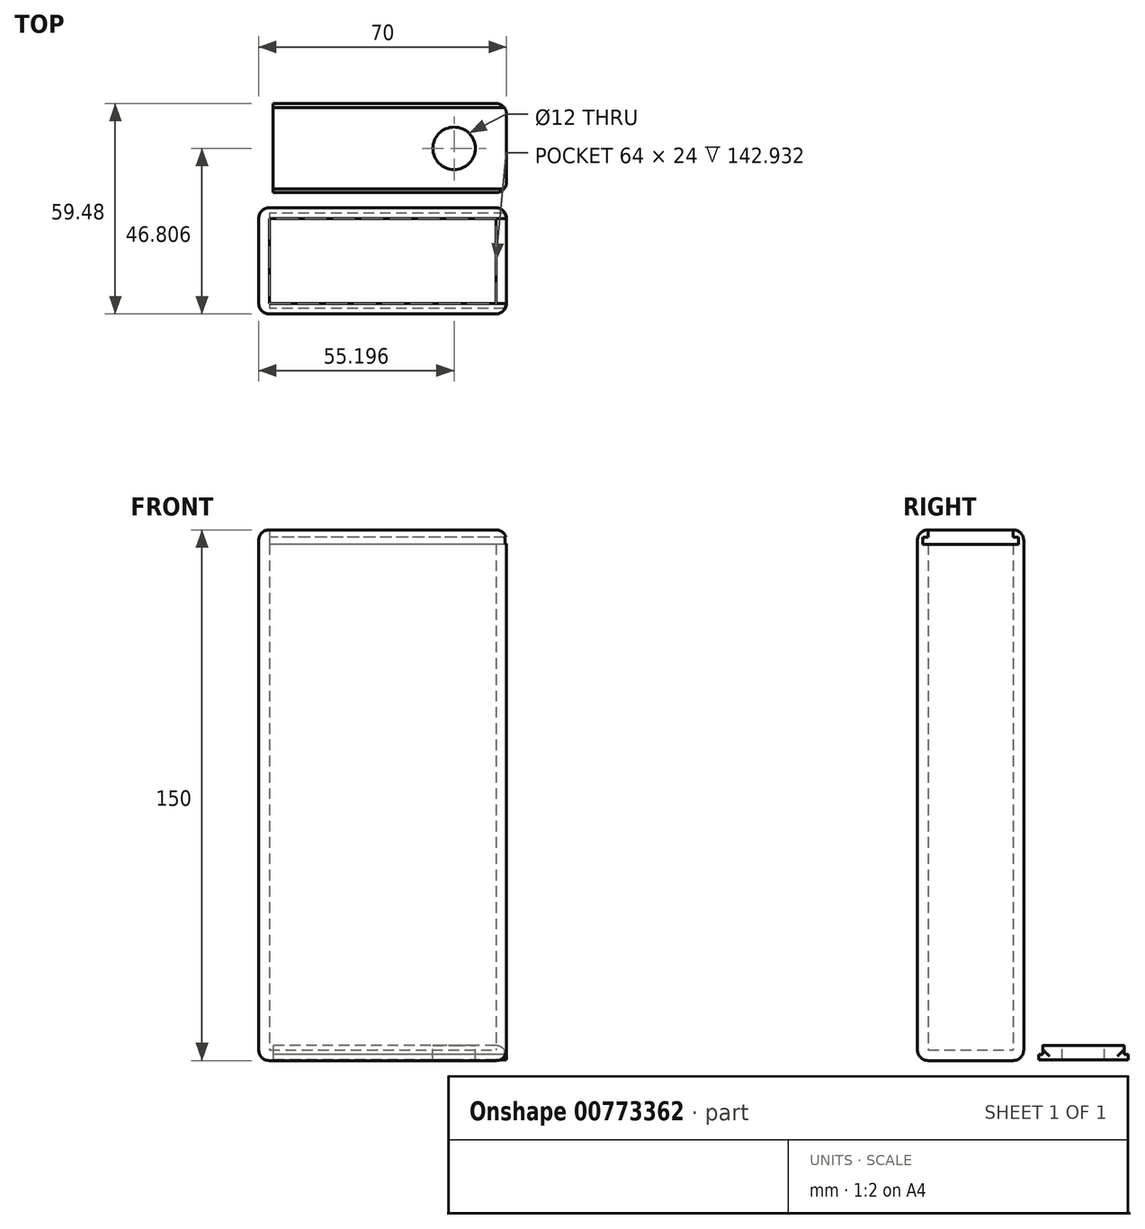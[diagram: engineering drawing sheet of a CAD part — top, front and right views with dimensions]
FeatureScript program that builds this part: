
annotation { "Feature Type Name" : "Feature", "Feature Type Description" : "" }
export const myFeature = defineFeature(function(context is Context, id is Id, definition is map)
    precondition{}
    {
        {
            var Q0;
            Q0=qCreatedBy(makeId("Top.planeOp"),FACE);
            var sketch = newSketch(context, id + "F0", { "sketchPlane" : qUnion([Q0])});
            skLineSegment(sketch, "E0.bottom", {"start": v(-35, -15) * mm, "end": v(35, -15) * mm});
            skLineSegment(sketch, "E0.top", {"start": v(-35, 15) * mm, "end": v(35, 15) * mm});
            skLineSegment(sketch, "E0.left", {"start": v(-35, -15) * mm, "end": v(-35, 15) * mm});
            skLineSegment(sketch, "E0.right", {"start": v(35, -15) * mm, "end": v(35, 15) * mm});
            skPoint(sketch, "E0.middle", {"position": v(0, 0) * mm});
            skSolve(sketch);
        }
        {
            var Q0;
            Q0 = qSketchRegion(id + "F0", true);
            extrude(context, id + "F1", {"entities" : qUnion([Q0]), "depth" : 150 * mm, "offsetDistance" : 25 * mm});
        }
        {
            var Q0;
            Q0=makeQuery(id+"F1.opExtrude","CAP_FACE",FACE,{"disambiguationData":[OSD([sQuery(id+"F0.wireOp",EDGE,"E0.bottom"),sQuery(id+"F0.wireOp",EDGE,"E0.top"),sQuery(id+"F0.wireOp",EDGE,"E0.left"),sQuery(id+"F0.wireOp",EDGE,"E0.right")])],"isStart":false});
            shell(context, id + "F2", {"entities" : qUnion([Q0]), "thickness" : 3 * mm});
        }
        {
            var Q0;
            Q0=qCreatedBy(makeId("Right.planeOp"),FACE);
            var sketch = newSketch(context, id + "F3", { "sketchPlane" : qUnion([Q0])});
            skLineSegment(sketch, "E1.bottom", {"start": v(12, 150.47) * mm, "end": v(-12, 150.47) * mm});
            skLineSegment(sketch, "E1.top", {"start": v(12, 147.47) * mm, "end": v(-12, 147.47) * mm});
            skLineSegment(sketch, "E1.left", {"start": v(12, 150.47) * mm, "end": v(12, 147.47) * mm});
            skLineSegment(sketch, "E1.right", {"start": v(-12, 150.47) * mm, "end": v(-12, 147.47) * mm});
            skPoint(sketch, "E1.middle", {"position": v(0, 148.97) * mm});
            skLineSegment(sketch, "E2.bottom", {"start": v(13.5, 147.93) * mm, "end": v(-13.5, 147.93) * mm});
            skLineSegment(sketch, "E2.top", {"start": v(13.5, 145.93) * mm, "end": v(-13.5, 145.93) * mm});
            skLineSegment(sketch, "E2.left", {"start": v(13.5, 147.93) * mm, "end": v(13.5, 145.93) * mm});
            skLineSegment(sketch, "E2.right", {"start": v(-13.5, 147.93) * mm, "end": v(-13.5, 145.93) * mm});
            skPoint(sketch, "E2.middle", {"position": v(0, 146.93) * mm});
            skSolve(sketch);
        }
        {
            var Q0;
            Q0 = qSketchRegion(id + "F3", true);
            extrude(context, id + "F4", {"entities" : qUnion([Q0]), "operationType" : NewBodyOperationType.REMOVE, "depth" : 36.4 * mm, "offsetDistance" : 25 * mm, "hasSecondDirection" : true, "secondDirectionOppositeDirection" : true, "secondDirectionDepth" : 32 * mm});
        }
        {
            var Q0;
            Q0=makeQuery(id+"F1.opExtrude","SWEPT_EDGE",EDGE,{"disambiguationData":[OSD([sQuery(id+"F0.wireOp",EDGE,"E0.top"),sQuery(id+"F0.wireOp",EDGE,"E0.right")])]});
            var Q1;
            Q1=makeQuery(id+"F1.opExtrude","SWEPT_EDGE",EDGE,{"disambiguationData":[OSD([sQuery(id+"F0.wireOp",EDGE,"E0.bottom"),sQuery(id+"F0.wireOp",EDGE,"E0.right")])]});
            var Q2;
            Q2=makeQuery(id+"F1.opExtrude","CAP_EDGE",EDGE,{"disambiguationData":[OSD([sQuery(id+"F0.wireOp",EDGE,"E0.right")])],"isStart":true});
            var Q3;
            Q3=makeQuery(id+"F1.opExtrude","CAP_FACE",FACE,{"disambiguationData":[OSD([sQuery(id+"F0.wireOp",EDGE,"E0.bottom"),sQuery(id+"F0.wireOp",EDGE,"E0.top"),sQuery(id+"F0.wireOp",EDGE,"E0.left"),sQuery(id+"F0.wireOp",EDGE,"E0.right")])],"isStart":true});
            var Q4;
            Q4=makeQuery(id+"F1.opExtrude","SWEPT_EDGE",EDGE,{"disambiguationData":[OSD([sQuery(id+"F0.wireOp",EDGE,"E0.top"),sQuery(id+"F0.wireOp",EDGE,"E0.left")])]});
            var Q5;
            Q5=makeQuery(id+"F1.opExtrude","SWEPT_EDGE",EDGE,{"disambiguationData":[OSD([sQuery(id+"F0.wireOp",EDGE,"E0.bottom"),sQuery(id+"F0.wireOp",EDGE,"E0.left")])]});
            fillet(context, id + "F5", {"entities" : qUnion([Q0, Q1, Q2, Q3, Q4, Q5]), "radius" : 3 * mm, "tangentPropagation" : true, "allowEdgeOverflow" : false});
        }
        {
            var Q0;
            Q0=makeQuery(id+"F1.opExtrude","CAP_EDGE",EDGE,{"disambiguationData":[OSD([sQuery(id+"F0.wireOp",EDGE,"E0.bottom")])],"isStart":false});
            fillet(context, id + "F6", {"entities" : qUnion([Q0]), "radius" : 3 * mm, "tangentPropagation" : true, "allowEdgeOverflow" : false});
        }
        {
            var Q0;
            Q0=qCreatedBy(makeId("Right.planeOp"),FACE);
            var sketch = newSketch(context, id + "F7", { "sketchPlane" : qUnion([Q0])});
            skLineSegment(sketch, "E3.bottom", {"start": v(43.38, 4.22) * mm, "end": v(20.38, 4.22) * mm});
            skLineSegment(sketch, "E3.top", {"start": v(43.38, 1.62) * mm, "end": v(20.38, 1.62) * mm});
            skLineSegment(sketch, "E3.left", {"start": v(43.38, 4.22) * mm, "end": v(43.38, 1.62) * mm});
            skLineSegment(sketch, "E3.right", {"start": v(20.38, 4.22) * mm, "end": v(20.38, 1.62) * mm});
            skPoint(sketch, "E3.middle", {"position": v(31.88, 2.92) * mm});
            skLineSegment(sketch, "E4.bottom", {"start": v(44.48, 1.67) * mm, "end": v(19.28, 1.67) * mm});
            skLineSegment(sketch, "E4.top", {"start": v(44.48, 0.27) * mm, "end": v(19.28, 0.27) * mm});
            skLineSegment(sketch, "E4.left", {"start": v(44.48, 1.67) * mm, "end": v(44.48, 0.27) * mm});
            skLineSegment(sketch, "E4.right", {"start": v(19.28, 1.67) * mm, "end": v(19.28, 0.27) * mm});
            skPoint(sketch, "E4.middle", {"position": v(31.88, 0.97) * mm});
            skSolve(sketch);
        }
        {
            var Q0;
            Q0 = qSketchRegion(id + "F7", true);
            extrude(context, id + "F8", {"entities" : qUnion([Q0]), "depth" : 35 * mm, "offsetDistance" : 25 * mm, "hasSecondDirection" : true, "secondDirectionOppositeDirection" : true, "secondDirectionDepth" : 31 * mm});
        }
        {
            var Q0;
            Q0=makeQuery(id+"F8.opExtrude","CAP_EDGE",EDGE,{"disambiguationData":[OSD([sQuery(id+"F7.wireOp",EDGE,"E3.bottom")])],"isStart":false});
            var Q1;
            Q1=makeQuery(id+"F8.opExtrude","CAP_EDGE",EDGE,{"disambiguationData":[OSD([sQuery(id+"F7.wireOp",EDGE,"E4.right")])],"isStart":false});
            var Q2;
            Q2=makeQuery(id+"F8.opExtrude","CAP_EDGE",EDGE,{"disambiguationData":[OSD([sQuery(id+"F7.wireOp",EDGE,"E4.left")])],"isStart":false});
            fillet(context, id + "F9", {"entities" : qUnion([Q0, Q1, Q2]), "radius" : 3 * mm, "tangentPropagation" : true, "allowEdgeOverflow" : false});
        }
        {
            var Q0;
            Q0=makeQuery(id+"F8.opExtrude","SWEPT_FACE",FACE,{"disambiguationData":[OSD([sQuery(id+"F7.wireOp",EDGE,"E3.bottom")])]});
            var sketch = newSketch(context, id + "F10", { "sketchPlane" : qUnion([Q0])});
            skCircle(sketch, "E5", {"center": v(20.2, 31.8) * mm, "radius": 6 * mm});
            skSolve(sketch);
        }
        {
            var Q0;
            Q0 = qSketchRegion(id + "F10", true);
            extrude(context, id + "F11", {"entities" : qUnion([Q0]), "operationType" : NewBodyOperationType.REMOVE, "endBound" : BoundingType.THROUGH_ALL, "oppositeDirection" : true, "depth" : 25 * mm, "offsetDistance" : 25 * mm});
        }
    });
